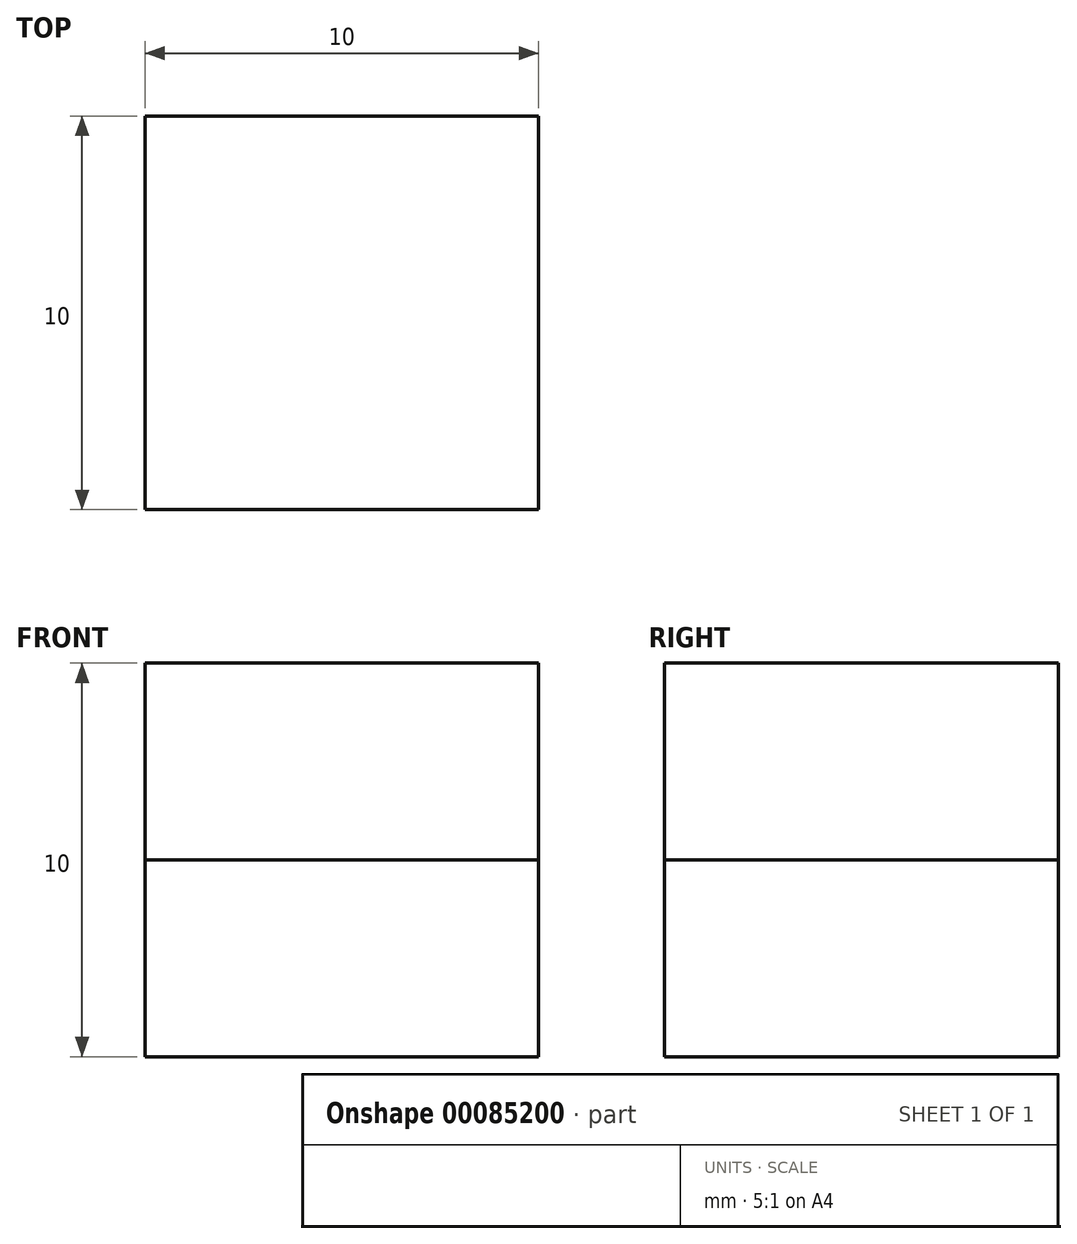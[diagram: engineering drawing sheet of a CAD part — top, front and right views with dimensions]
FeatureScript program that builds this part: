
annotation { "Feature Type Name" : "Feature", "Feature Type Description" : "" }
export const myFeature = defineFeature(function(context is Context, id is Id, definition is map)
    precondition{}
    {
        {
            var Q0;
            Q0=qCreatedBy(makeId("Front.planeOp"),FACE);
            var sketch = newSketch(context, id + "F0", { "sketchPlane" : qUnion([Q0])});
            skLineSegment(sketch, "E0.bottom", {"start": v(5, -5) * mm, "end": v(-5, -5) * mm});
            skLineSegment(sketch, "E0.top", {"start": v(5, 5) * mm, "end": v(-5, 5) * mm});
            skLineSegment(sketch, "E0.left", {"start": v(5, -5) * mm, "end": v(5, 5) * mm});
            skLineSegment(sketch, "E0.right", {"start": v(-5, -5) * mm, "end": v(-5, 5) * mm});
            skPoint(sketch, "E0.middle", {"position": v(0, 0) * mm});
            skLineSegment(sketch, "E1", {"start": v(-5, 0) * mm, "end": v(5, 0) * mm});
            skSolve(sketch);
        }
        {
            var Q0;
            {var subQ0=sQuery(id+"F0.wireOp",EDGE,"E0.bottom");Q0=makeQuery(id+"F0.imprint","IMPRINT",FACE,{"disambiguationData":[TD([[makeQuery(id+"F0.imprint","IMPRINT",EDGE,{"derivedFrom":subQ0}),-1.0]])]});}
            extrude(context, id + "F1", {"entities" : qUnion([Q0]), "depth" : 10 * mm});
        }
        {
            var Q0;
            {var subQ0=sQuery(id+"F0.wireOp",EDGE,"E0.top");Q0=makeQuery(id+"F0.imprint","IMPRINT",FACE,{"disambiguationData":[TD([[makeQuery(id+"F0.imprint","IMPRINT",EDGE,{"derivedFrom":subQ0}),1.0]])]});}
            extrude(context, id + "F2", {"entities" : qUnion([Q0]), "depth" : 10 * mm});
        }
    });
